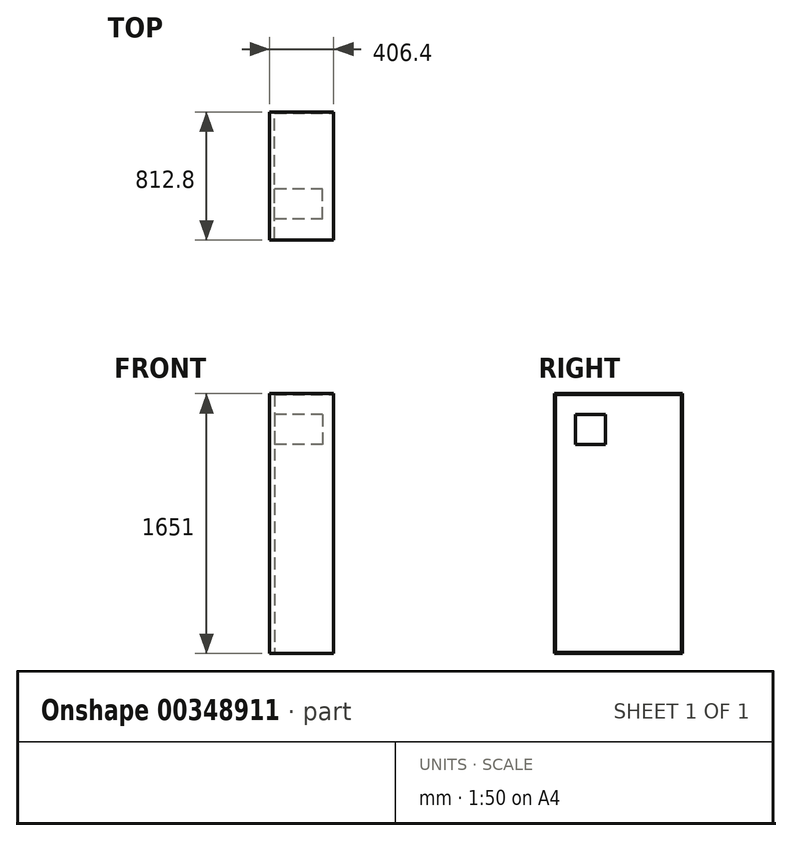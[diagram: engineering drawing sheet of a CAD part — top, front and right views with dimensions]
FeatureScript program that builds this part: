
annotation { "Feature Type Name" : "Feature", "Feature Type Description" : "" }
export const myFeature = defineFeature(function(context is Context, id is Id, definition is map)
    precondition{}
    {
        {
            var Q0;
            Q0=qCreatedBy(makeId("Top.planeOp"),FACE);
            var sketch = newSketch(context, id + "F0", { "sketchPlane" : qUnion([Q0])});
            skLineSegment(sketch, "E0.bottom", {"start": v(0, 0) * mm, "end": v(406.4, 0) * mm});
            skLineSegment(sketch, "E0.top", {"start": v(0, 812.8) * mm, "end": v(406.4, 812.8) * mm});
            skLineSegment(sketch, "E0.left", {"start": v(0, 0) * mm, "end": v(0, 812.8) * mm});
            skLineSegment(sketch, "E0.right", {"start": v(406.4, 0) * mm, "end": v(406.4, 812.8) * mm});
            skSolve(sketch);
        }
        {
            var Q0;
            Q0 = qSketchRegion(id + "F0", true);
            extrude(context, id + "F1", {"entities" : qUnion([Q0]), "depth" : 1651 * mm});
        }
        {
            var Q0;
            Q0=makeQuery(id+"F1.opExtrude","SWEPT_FACE",FACE,{"disambiguationData":[OSD([sQuery(id+"F0.wireOp",EDGE,"E0.right")])]});
            shell(context, id + "F2", {"entities" : qUnion([Q0]), "thickness" : 6.35 * mm});
        }
        {
            var Q0;
            Q0=makeQuery(id+"F2.opShell","OFFSET_FACE",FACE,{"disambiguationData":[OSD([sQuery(id+"F0.wireOp",EDGE,"E0.left")])]});
            extrude(context, id + "F3", {"entities" : qUnion([Q0]), "operationType" : NewBodyOperationType.ADD, "depth" : 25.4 * mm});
        }
        {
            var Q0;
            Q0=makeQuery(id+"F3.opExtrude","CAP_FACE",FACE,{"disambiguationData":[OSD([sQuery(id+"F0.wireOp",EDGE,"E0.left")])],"isStart":false});
            var sketch = newSketch(context, id + "F4", { "sketchPlane" : qUnion([Q0])});
            skLineSegment(sketch, "E1.bottom", {"start": v(133.35, 1517.65) * mm, "end": v(323.85, 1517.65) * mm});
            skLineSegment(sketch, "E1.top", {"start": v(133.35, 1327.15) * mm, "end": v(323.85, 1327.15) * mm});
            skLineSegment(sketch, "E1.left", {"start": v(133.35, 1517.65) * mm, "end": v(133.35, 1327.15) * mm});
            skLineSegment(sketch, "E1.right", {"start": v(323.85, 1517.65) * mm, "end": v(323.85, 1327.15) * mm});
            skSolve(sketch);
        }
        {
            var Q0;
            Q0=makeQuery(id+"F4.imprint","IMPRINT",FACE,{"disambiguationData":[TD([[makeQuery(id+"F4.imprint","IMPRINT",EDGE,{"derivedFrom":sQuery(id+"F4.wireOp",EDGE,"E1.bottom")}),-1.0]])]});
            extrude(context, id + "F5", {"entities" : qUnion([Q0]), "operationType" : NewBodyOperationType.ADD, "depth" : 304.8 * mm});
        }
    });
